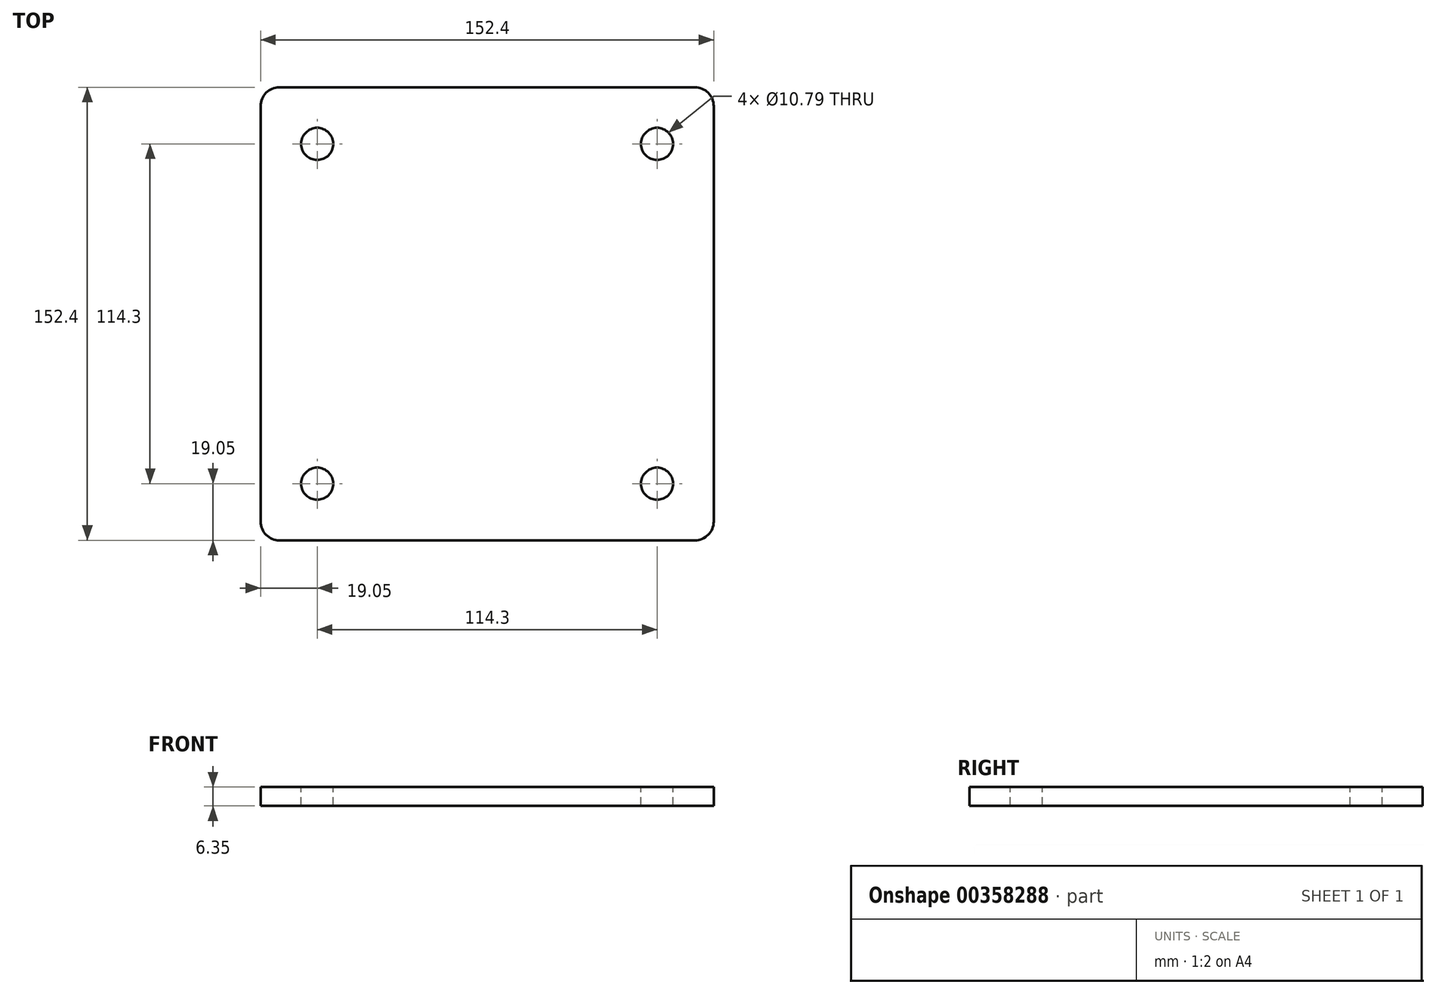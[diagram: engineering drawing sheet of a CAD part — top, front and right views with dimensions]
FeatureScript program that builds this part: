
annotation { "Feature Type Name" : "Feature", "Feature Type Description" : "" }
export const myFeature = defineFeature(function(context is Context, id is Id, definition is map)
    precondition{}
    {
        {
            var Q0;
            Q0=qCreatedBy(makeId("Top.planeOp"),FACE);
            var sketch = newSketch(context, id + "F0", { "sketchPlane" : qUnion([Q0])});
            skLineSegment(sketch, "E0.bottom", {"start": v(6.35, 0) * mm, "end": v(146.05, 0) * mm});
            skLineSegment(sketch, "E0.top", {"start": v(6.35, -152.4) * mm, "end": v(146.05, -152.4) * mm});
            skLineSegment(sketch, "E0.left", {"start": v(0, -6.35) * mm, "end": v(0, -146.05) * mm});
            skLineSegment(sketch, "E0.right", {"start": v(152.4, -6.35) * mm, "end": v(152.4, -146.05) * mm});
            skPoint(sketch, "E1.visualSharp", {"position": v(0, 0) * mm});
            skArc(sketch, "E1.filletArc", {"start": v(6.35, 0) * mm, "mid": v(1.86, -1.86) * mm, "end": v(0, -6.35) * mm});
            skPoint(sketch, "E2.visualSharp", {"position": v(152.4, 0) * mm});
            skArc(sketch, "E2.filletArc", {"start": v(152.4, -6.35) * mm, "mid": v(150.54, -1.86) * mm, "end": v(146.05, 0) * mm});
            skPoint(sketch, "E3.visualSharp", {"position": v(152.4, -152.4) * mm});
            skArc(sketch, "E3.filletArc", {"start": v(146.05, -152.4) * mm, "mid": v(150.54, -150.54) * mm, "end": v(152.4, -146.05) * mm});
            skPoint(sketch, "E4.visualSharp", {"position": v(0, -152.4) * mm});
            skArc(sketch, "E4.filletArc", {"start": v(0, -146.05) * mm, "mid": v(1.86, -150.54) * mm, "end": v(6.35, -152.4) * mm});
            skSolve(sketch);
        }
        {
            var Q0;
            Q0=makeQuery(id+"F0.imprint","IMPRINT",FACE,{"disambiguationData":[TD([[makeQuery(id+"F0.imprint","IMPRINT",EDGE,{"derivedFrom":sQuery(id+"F0.wireOp",EDGE,"E0.bottom")}),-1.0]])]});
            extrude(context, id + "F1", {"entities" : qUnion([Q0]), "depth" : 6.35 * mm});
        }
        {
            var Q0;
            Q0=makeQuery(id+"F1.opExtrude","CAP_FACE",FACE,{"disambiguationData":[OSD([sQuery(id+"F0.wireOp",EDGE,"E0.bottom"),sQuery(id+"F0.wireOp",EDGE,"E0.top"),sQuery(id+"F0.wireOp",EDGE,"E0.left"),sQuery(id+"F0.wireOp",EDGE,"E0.right"),sQuery(id+"F0.wireOp",EDGE,"E1.filletArc"),sQuery(id+"F0.wireOp",EDGE,"E2.filletArc"),sQuery(id+"F0.wireOp",EDGE,"E3.filletArc"),sQuery(id+"F0.wireOp",EDGE,"E4.filletArc")])],"isStart":false});
            var sketch = newSketch(context, id + "F2", { "sketchPlane" : qUnion([Q0])});
            skCircle(sketch, "E5", {"center": v(133.35, -19.05) * mm, "radius": 5.4 * mm});
            skCircle(sketch, "E6.0.1.0", {"center": v(133.35, -133.35) * mm, "radius": 5.4 * mm});
            skCircle(sketch, "E6.1.0.0", {"center": v(19.05, -19.05) * mm, "radius": 5.4 * mm});
            skCircle(sketch, "E6.1.1.0", {"center": v(19.05, -133.35) * mm, "radius": 5.4 * mm});
            skLineSegment(sketch, "E6.direction1", {"start": v(133.35, -19.05) * mm, "end": v(19.05, -19.05) * mm, "construction": true});
            skLineSegment(sketch, "E6.direction2", {"start": v(133.35, -19.05) * mm, "end": v(133.35, -133.35) * mm, "construction": true});
            skSolve(sketch);
        }
        {
            var Q0;
            Q0 = qSketchRegion(id + "F2", true);
            extrude(context, id + "F3", {"entities" : qUnion([Q0]), "operationType" : NewBodyOperationType.REMOVE, "oppositeDirection" : true, "depth" : 6.35 * mm});
        }
    });
